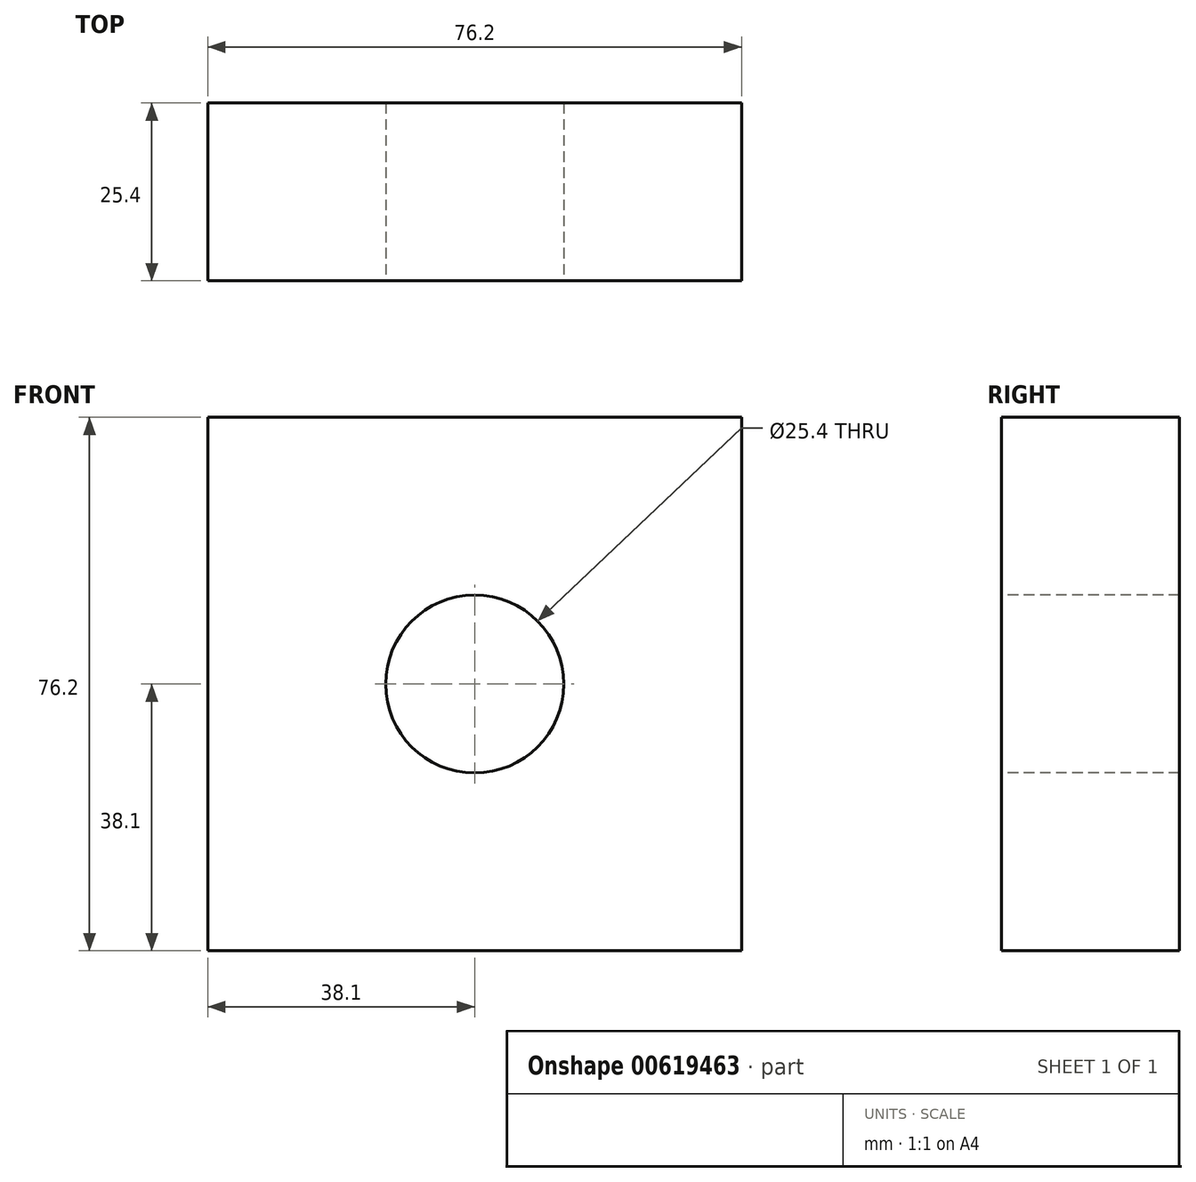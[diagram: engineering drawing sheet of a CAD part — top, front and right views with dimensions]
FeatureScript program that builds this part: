
annotation { "Feature Type Name" : "Feature", "Feature Type Description" : "" }
export const myFeature = defineFeature(function(context is Context, id is Id, definition is map)
    precondition{}
    {
        {
            var Q0;
            Q0=qCreatedBy(makeId("Front.planeOp"),FACE);
            var sketch = newSketch(context, id + "F0", { "sketchPlane" : qUnion([Q0])});
            skLineSegment(sketch, "E0.bottom", {"start": v(-38.1, 38.1) * mm, "end": v(38.1, 38.1) * mm});
            skLineSegment(sketch, "E0.top", {"start": v(-38.1, -38.1) * mm, "end": v(38.1, -38.1) * mm});
            skLineSegment(sketch, "E0.left", {"start": v(-38.1, 38.1) * mm, "end": v(-38.1, -38.1) * mm});
            skLineSegment(sketch, "E0.right", {"start": v(38.1, 38.1) * mm, "end": v(38.1, -38.1) * mm});
            skPoint(sketch, "E0.middle", {"position": v(0, 0) * mm});
            skCircle(sketch, "E1", {"center": v(0, 0) * mm, "radius": 12.7 * mm});
            skSolve(sketch);
        }
        {
            var Q0;
            Q0=makeQuery(id+"F0.imprint","IMPRINT",FACE,{"disambiguationData":[TD([[makeQuery(id+"F0.imprint","IMPRINT",EDGE,{"derivedFrom":sQuery(id+"F0.wireOp",EDGE,"E0.bottom")}),-1.0]])]});
            extrude(context, id + "F1", {"entities" : qUnion([Q0]), "oppositeDirection" : true, "depth" : 25.4 * mm, "offsetDistance" : 25.4 * mm});
        }
    });
